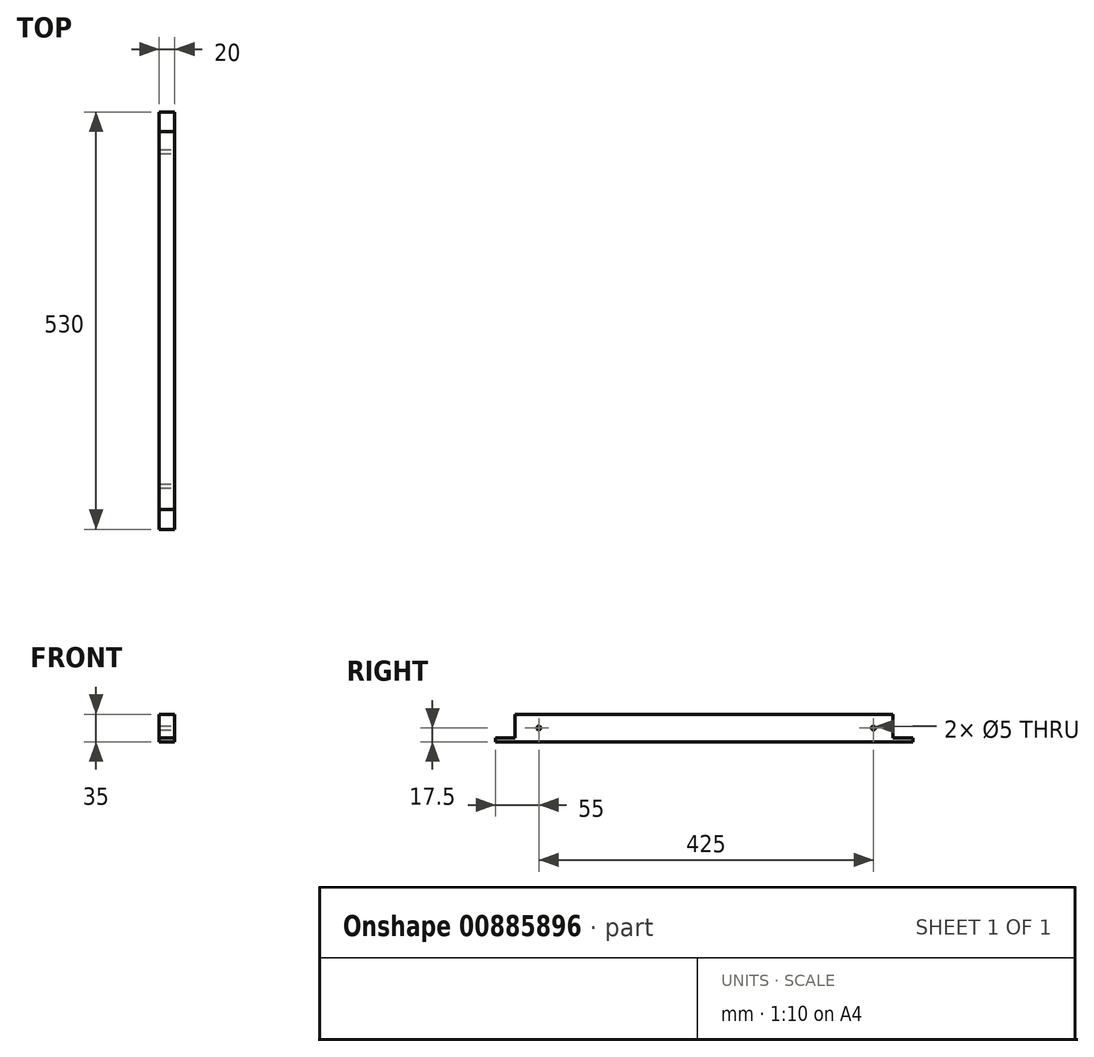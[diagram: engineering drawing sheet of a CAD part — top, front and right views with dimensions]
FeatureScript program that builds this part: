
annotation { "Feature Type Name" : "Feature", "Feature Type Description" : "" }
export const myFeature = defineFeature(function(context is Context, id is Id, definition is map)
    precondition{}
    {
        {
            var Q0;
            Q0=qCreatedBy(makeId("Front.planeOp"),FACE);
            var sketch = newSketch(context, id + "F0", { "sketchPlane" : qUnion([Q0])});
            skLineSegment(sketch, "E0.bottom", {"start": v(10, 17.5) * mm, "end": v(-10, 17.5) * mm});
            skLineSegment(sketch, "E0.top", {"start": v(10, -17.5) * mm, "end": v(-10, -17.5) * mm});
            skLineSegment(sketch, "E0.left", {"start": v(10, 17.5) * mm, "end": v(10, -17.5) * mm});
            skLineSegment(sketch, "E0.right", {"start": v(-10, 17.5) * mm, "end": v(-10, -17.5) * mm});
            skPoint(sketch, "E0.middle", {"position": v(0, 0) * mm});
            skSolve(sketch);
        }
        {
            var Q0;
            Q0 = qSketchRegion(id + "F0", true);
            extrude(context, id + "F1", {"entities" : qUnion([Q0]), "oppositeDirection" : true, "depth" : 530 * mm, "offsetDistance" : 25 * mm});
        }
        {
            var Q0;
            Q0=makeQuery(id+"F1.opExtrude","SWEPT_FACE",FACE,{"disambiguationData":[OSD([sQuery(id+"F0.wireOp",EDGE,"E0.left")])]});
            var sketch = newSketch(context, id + "F2", { "sketchPlane" : qUnion([Q0])});
            skLineSegment(sketch, "E1.bottom", {"start": v(0, 17.5) * mm, "end": v(25, 17.5) * mm});
            skLineSegment(sketch, "E1.top", {"start": v(0, -12.5) * mm, "end": v(25, -12.5) * mm});
            skLineSegment(sketch, "E1.left", {"start": v(0, 17.5) * mm, "end": v(0, -12.5) * mm});
            skLineSegment(sketch, "E1.right", {"start": v(25, 17.5) * mm, "end": v(25, -12.5) * mm});
            skLineSegment(sketch, "E2.bottom", {"start": v(530, 17.5) * mm, "end": v(505, 17.5) * mm});
            skLineSegment(sketch, "E2.top", {"start": v(530, -12.5) * mm, "end": v(505, -12.5) * mm});
            skLineSegment(sketch, "E2.left", {"start": v(530, 17.5) * mm, "end": v(530, -12.5) * mm});
            skLineSegment(sketch, "E2.right", {"start": v(505, 17.5) * mm, "end": v(505, -12.5) * mm});
            skSolve(sketch);
        }
        {
            var Q0;
            Q0 = qSketchRegion(id + "F2", true);
            extrude(context, id + "F3", {"entities" : qUnion([Q0]), "operationType" : NewBodyOperationType.REMOVE, "oppositeDirection" : true, "depth" : 20 * mm, "offsetDistance" : 25 * mm});
        }
        {
            var Q0;
            Q0=makeQuery(id+"F1.opExtrude","SWEPT_FACE",FACE,{"disambiguationData":[OSD([sQuery(id+"F0.wireOp",EDGE,"E0.left")])]});
            var sketch = newSketch(context, id + "F4", { "sketchPlane" : qUnion([Q0])});
            skCircle(sketch, "E3", {"center": v(55, 0) * mm, "radius": 2.5 * mm});
            skCircle(sketch, "E4", {"center": v(480, 0) * mm, "radius": 2.5 * mm});
            skSolve(sketch);
        }
        {
            var Q0;
            Q0 = qSketchRegion(id + "F4", true);
            extrude(context, id + "F5", {"entities" : qUnion([Q0]), "operationType" : NewBodyOperationType.REMOVE, "oppositeDirection" : true, "depth" : 25 * mm, "offsetDistance" : 25 * mm});
        }
    });
